# Revit family: flat_slim_round_312135_0031_2_8808
name_source: partatom
category: Lighting Fixtures
units: mm (PartAtom-declared; Revit-internal decimal feet)

## family parameters
Cut with Voids When Loaded = No
Host = Face
Light Source = No
Part Type = Normal
Room Calculation Point = No
Round Connector Dimension = Use Diameter
Shared = No

## types (1)
- FLAT SLIM round (1 x LED Modul 830, 1300 lm, 3000)
    Apparent Load = 12 VA
    CIE Flux Codes = 43 74 92 91 100
    Color Rendering = 80
    Color Temperature = 3000
    Default Elevation = 1800 mm
    Height = 63 mm
    Lamp = 1 x LED Modul 830
    Lamp Light Flux = 1300 lm
    Lamp count = 1
    Length = 230 mm
    Lifetime = 50000 h
    Luminous efficacy = 108 lm/W
    Manufacturer = RZB
    ModVariant = No
    Model = 312135.0031.2
    Mounting Place = Wall, Ceiling
    Mounting Type = Surface mounted
    Number of Poles = 1
    OnlyDefault = Yes
    Power Factor = 1
    Product Name = FLAT SLIM round
    Product group = Surface mounted ceiling and wall luminaires
    ProductGroupID = 305
    Protection Class = Protection class I
    Protection Degree = IP 65
    RLX_Detail_Level = 1
    RLX_Emergency_Light_Flux = 0 lm
    RLX_Emergency_Type = 0
    RLX_Emergency_Type_DB = No
    RlxData = <blob elided: 17673 chars, md5=9e288bd2>
    Socket = socket
    Standby Power = 0 W
    System Light Flux = 1300 lm
    System Power = 12 W
    Type Comments = Product without accessories
    Type Image = 312132.0031.jpg
    URL = http://relux.com
    VarID = ---
    Voltage = 230 V
    Voltage Range = 220-240 V
    Weight = 0.00 kg
    Width = 0 mm  [stored 0 ft]

note: [stored X ft] marks values corroborated as IEEE doubles in the binary element streams (Revit-internal decimal feet)

## geometry (parser evidence)
native form markers: Blend x4, Sweep x14
no freeform markers — native parametric forms only
